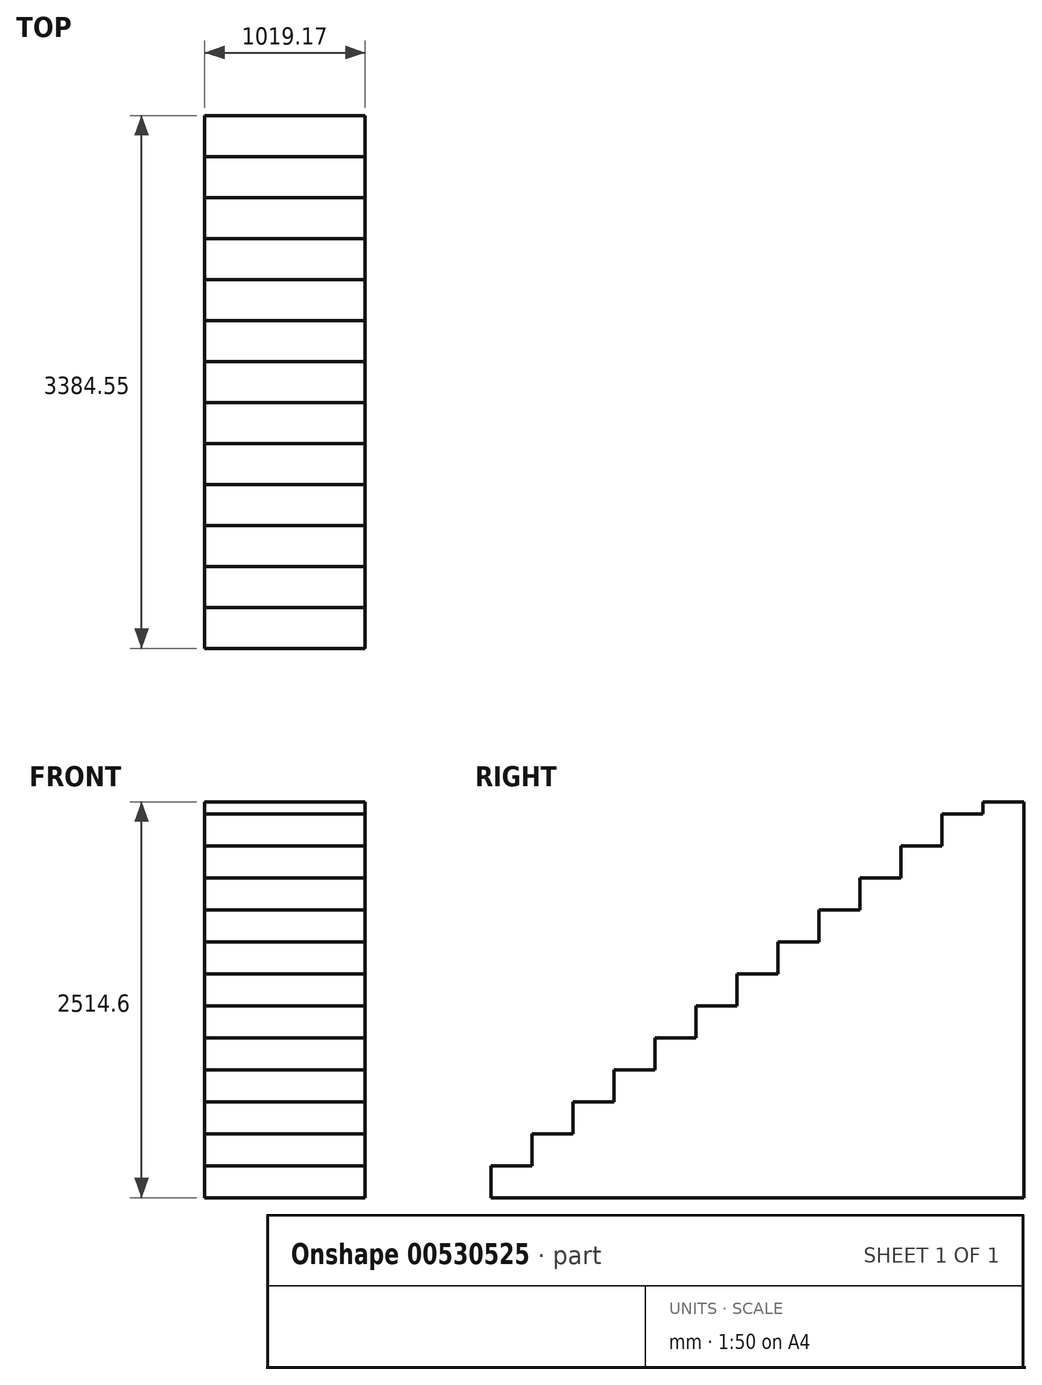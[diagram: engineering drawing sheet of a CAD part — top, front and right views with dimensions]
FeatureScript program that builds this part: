
annotation { "Feature Type Name" : "Feature", "Feature Type Description" : "" }
export const myFeature = defineFeature(function(context is Context, id is Id, definition is map)
    precondition{}
    {
        {
            var Q0;
            Q0=qCreatedBy(makeId("Top.planeOp"),FACE);
            var sketch = newSketch(context, id + "F0", { "sketchPlane" : qUnion([Q0])});
            skLineSegment(sketch, "E0.bottom", {"start": v(0, 0) * mm, "end": v(1019.17, 0) * mm});
            skLineSegment(sketch, "E0.top", {"start": v(0, 3384.55) * mm, "end": v(1019.17, 3384.55) * mm});
            skLineSegment(sketch, "E0.left", {"start": v(0, 0) * mm, "end": v(0, 3384.55) * mm});
            skLineSegment(sketch, "E0.right", {"start": v(1019.18, 0) * mm, "end": v(1019.18, 3384.55) * mm});
            skSolve(sketch);
        }
        {
            var Q0;
            Q0 = qSketchRegion(id + "F0", true);
            extrude(context, id + "F1", {"entities" : qUnion([Q0]), "depth" : 2514.6 * mm, "offsetDistance" : 25.4 * mm});
        }
        {
            var Q0;
            Q0=makeQuery(id+"F1.opExtrude","SWEPT_FACE",FACE,{"disambiguationData":[OSD([sQuery(id+"F0.wireOp",EDGE,"E0.left")])]});
            var sketch = newSketch(context, id + "F2", { "sketchPlane" : qUnion([Q0])});
            skLineSegment(sketch, "E1", {"start": v(0, 0) * mm, "end": v(0, 203.2) * mm});
            skLineSegment(sketch, "E2", {"start": v(0, 203.2) * mm, "end": v(-260.35, 203.2) * mm});
            skLineSegment(sketch, "E3", {"start": v(-260.35, 203.2) * mm, "end": v(-260.35, 406.4) * mm});
            skLineSegment(sketch, "E4", {"start": v(-260.35, 406.4) * mm, "end": v(-520.7, 406.4) * mm});
            skLineSegment(sketch, "E5", {"start": v(-520.7, 406.4) * mm, "end": v(-520.7, 609.6) * mm});
            skLineSegment(sketch, "E6", {"start": v(-520.7, 609.6) * mm, "end": v(-781.05, 609.6) * mm});
            skLineSegment(sketch, "E7", {"start": v(-781.05, 609.6) * mm, "end": v(-781.05, 812.8) * mm});
            skLineSegment(sketch, "E8", {"start": v(-781.05, 812.8) * mm, "end": v(-1041.4, 812.8) * mm});
            skLineSegment(sketch, "E9", {"start": v(-1041.4, 812.8) * mm, "end": v(-1041.4, 1016) * mm});
            skLineSegment(sketch, "E10", {"start": v(-1041.4, 1016) * mm, "end": v(-1301.75, 1016) * mm});
            skLineSegment(sketch, "E11", {"start": v(-1301.75, 1016) * mm, "end": v(-1301.75, 1219.2) * mm});
            skLineSegment(sketch, "E12", {"start": v(-1301.75, 1219.2) * mm, "end": v(-1562.1, 1219.2) * mm});
            skLineSegment(sketch, "E13", {"start": v(-1562.1, 1219.2) * mm, "end": v(-1562.1, 1422.4) * mm});
            skLineSegment(sketch, "E14", {"start": v(-1562.1, 1422.4) * mm, "end": v(-1822.45, 1422.4) * mm});
            skLineSegment(sketch, "E15", {"start": v(-1822.45, 1422.4) * mm, "end": v(-1822.45, 1625.6) * mm});
            skLineSegment(sketch, "E16", {"start": v(-1822.45, 1625.6) * mm, "end": v(-2082.8, 1625.6) * mm});
            skLineSegment(sketch, "E17", {"start": v(-2082.8, 1625.6) * mm, "end": v(-2082.8, 1828.8) * mm});
            skLineSegment(sketch, "E18", {"start": v(-2082.8, 1828.8) * mm, "end": v(-2343.15, 1828.8) * mm});
            skLineSegment(sketch, "E19", {"start": v(-2343.15, 1828.8) * mm, "end": v(-2343.15, 2032) * mm});
            skLineSegment(sketch, "E20", {"start": v(-2343.15, 2032) * mm, "end": v(-2603.5, 2032) * mm});
            skLineSegment(sketch, "E21", {"start": v(-2603.5, 2032) * mm, "end": v(-2603.5, 2235.2) * mm});
            skLineSegment(sketch, "E22", {"start": v(-2603.5, 2235.2) * mm, "end": v(-2863.85, 2235.2) * mm});
            skLineSegment(sketch, "E23", {"start": v(-2863.85, 2235.2) * mm, "end": v(-2863.85, 2438.4) * mm});
            skLineSegment(sketch, "E24", {"start": v(-2863.85, 2438.4) * mm, "end": v(-3124.2, 2438.4) * mm});
            skLineSegment(sketch, "E25", {"start": v(-3124.2, 2438.4) * mm, "end": v(-3124.2, 2641.6) * mm});
            skLineSegment(sketch, "E26", {"start": v(-3124.2, 2641.6) * mm, "end": v(-3384.55, 2641.6) * mm});
            skLineSegment(sketch, "E27", {"start": v(-3384.55, 2641.6) * mm, "end": v(-3384.55, 2844.8) * mm});
            skLineSegment(sketch, "E28", {"start": v(-3384.55, 2844.8) * mm, "end": v(-3384.55, 2844.8) * mm});
            skSolve(sketch);
        }
        {
            var Q0;
            {var subQ0=sQuery(id+"F2.wireOp",EDGE,"E2");Q0=makeQuery(id+"F2.imprint","IMPRINT",FACE,{"disambiguationData":[TD([[makeQuery(id+"F2.imprint","IMPRINT",EDGE,{"derivedFrom":subQ0}),-1.0]])]});}
            extrude(context, id + "F3", {"entities" : qUnion([Q0]), "operationType" : NewBodyOperationType.REMOVE, "oppositeDirection" : true, "depth" : 1019.17 * mm, "offsetDistance" : 25.4 * mm});
        }
    });
